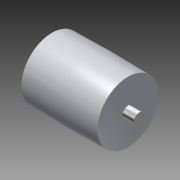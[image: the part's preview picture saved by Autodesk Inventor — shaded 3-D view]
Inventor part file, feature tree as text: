
AUTODESK INVENTOR PART (.ipt)
format: ipt  version: 2014 (Build 180170000, 170)  size: 103,424 bytes
history: native  units: in
note: dims shown in document units (in); Inventor stores cm internally (conversion verified against a paired STEP export)
features: revolve x1, sketch x1
ambient origin geometry x8: Origin, YZ Plane, XZ Plane, XY Plane, X Axis, Y Axis, Z Axis, Center Point
bodies: Solid1 (feature_tree)
feature tree (2):
  revolve  "Revolution1"  [1 undecoded]
  sketch  "Sketch1"  dims[d0=0.58in d1=0.032in d2=0.182in d3=0.179in d4=0.446in d5=0.067in d6=0.067in d7=90.0deg]
note: 1 required parameter value undecoded (feature->parameter linkage not recoverable at this tier; creation-order binding heuristic only, values carry confidence <= 0.55)
